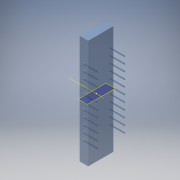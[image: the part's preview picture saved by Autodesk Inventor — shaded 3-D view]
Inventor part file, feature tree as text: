
AUTODESK INVENTOR PART (.ipt)
format: ipt  version: 2017 (Build 210142000, 142)  size: 243,200 bytes
history: native  units: mm
features: sketch x5, extrude x4, plane x2, chamfer x1, other x1, pattern_linear x1
ambient origin geometry x8: Origin, YZ Plane, XZ Plane, XY Plane, X Axis, Y Axis, Z Axis, Center Point
bodies: Solid1 (feature_tree)
feature tree (14):
  extrude  "Extrusion1"  Depth=41.6mm
  extrude  "Extrusion2"  Depth=3.22mm
  chamfer  "Chamfer1"  Distance=1.52mm
  sketch  "Sketch3"  dims[d5=1.0mm d6=1.52mm d7=0.0mm]
  other  "Work Axis1"
  plane  "Work Plane1"
  extrude  "Extrusion3"  Depth=0.25mm
  pattern_linear  "Rectangular Pattern1"  Spacing1=10.1mm  [1 undecoded]
  plane  "Work Plane2"
  extrude  "Extrusion4"  Depth=0.25mm
  sketch  "Sketch1"  dims[d0=9.65mm d1=41.6mm]
  sketch  "Sketch2"  dims[d2=3.22mm d3=0.0mm d4=29.1mm]
  sketch  "Sketch4"  dims[d8=1.52mm d9=2.0mm d10=45.0deg d11=0.25mm]
  sketch  "Sketch5"  dims[d13=4.0mm d15=10.1mm d16=0.25mm d17=0.47mm d18=0.0mm d19=110.0mm d21=2.54mm d22=3.0mm d23=0.47mm d24=0.0mm]
note: 1 required parameter value undecoded (feature->parameter linkage not recoverable at this tier; creation-order binding heuristic only, values carry confidence <= 0.55)
